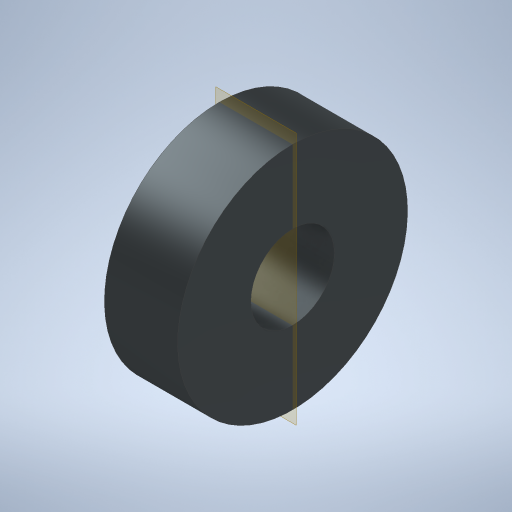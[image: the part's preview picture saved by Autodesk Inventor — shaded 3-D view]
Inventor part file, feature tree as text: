
AUTODESK INVENTOR PART (.ipt)
format: ipt  version: 2023 (Build 270158000, 158)  size: 249,344 bytes
history: native  units: mm
features: extrude x2, sketch x2, plane x1
ambient origin geometry x8: Origin, YZ Plane, XZ Plane, XY Plane, X Axis, Y Axis, Z Axis, Center Point
bodies: Volumenkörper1 (feature_tree)
feature tree (5):
  extrude  "Extrusion1"  Depth=7.0mm TaperAngle=0.0deg
  extrude  "Extrusion2"  TaperAngle=0.0deg  [1 undecoded]
  plane  "Arbeitsebene1"
  sketch  "Skizze1"  dims[d0=22.0mm d1=7.0mm d2=0.0mm]
  sketch  "Skizze2"  dims[d3=8.0mm d4=0.0mm d5=0.0mm d6=0.0mm]
note: 1 required parameter value undecoded (feature->parameter linkage not recoverable at this tier; creation-order binding heuristic only, values carry confidence <= 0.55)
